# Revit family: Bath&ShowerMixer-(Built-in)-Vitra-JunoSeries-A40868
name_source: partatom
category: Plumbing Fixtures
revit_build: Autodesk Revit 2017 (Build: 20160225_1515(x64)
units: mm (PartAtom-declared; Revit-internal decimal feet)

## family parameters
Cut with Voids When Loaded = No
Host = Face
OmniClass Number = 23.45.00.00
OmniClass Title = Sanitary, Laundry, and Cleaning Equipment
Part Type = Normal
Room Calculation Point = No
Round Connector Dimension = Use Diameter
Shared = Yes

## types (3) — shared parameters
BIMobject category = Bath/Shower Mixer
Brand = VitrA
CW Connection = Yes
Connection Diameter (mm) = 15 mm
Default Elevation = 850 mm
Description = Juno Bath/Shower Mixer
Design country = Turkey
HW Connection = Yes
Hot Water Supply (max.) = 80 °C
Hot Water temperature, factory set to = 38 °C
IFC Classification = Sanitary Terminal
Main Material = Brass
Manufacturer = Vitra
Manufacturer name = Vitra
Masterformat 2014 Code = 22 40 00
Masterformat 2014 Description = Plumbing Fixtures
Min. flow pressure of = 0.5 bar
Mounting type = Built-In
NBS Referans Code = 45-35-70/315
NBS Referans Description = Water supply fittings for baths
Nominal Depth (mm) = 200 mm  [stored 0.656168 ft]
Nominal Height (mm) = 106 mm  [stored 0.347769 ft]
Nominal Width (mm) = 220 mm  [stored 0.721785 ft]
Number Of Connections = 2
OmniClass Code = 23.45.55.17
OmniClass Description = Mixing Faucets
Primary Material = <By Category>
Product Properties = Energy Saving
Product Type = Bath&Shower Mixer
Product certification = https://www.vitraglobal.com
Product family = Juno
Product group = Juno Bath&Shower Mixer
Product url = https://www.vitra.com.tr
Range of Hot Water Supply = 5 - 65 °C
Range of flow pressure = 1 - 5 bar
Technical description = https://www.vitra.com.tr
Test Pressure = 16 bar
URL = https://vitraglobal.com
Uniclass 1.4 Code = L725111
Uniclass 1.4 Description = Mixer taps
Uniclass 2.0 Code = Pr_40_20_87_09
Uniclass 2.0 Description = Bath taps
Uniclass 2015 Code = Pr_40_20_87_09
Uniclass 2015 Name = Bath taps
Uniformat II Code = 22 40 00
Uniformat II Description = Plumbing Fixture
Vent Connection = No
Warranty Period (Year) = 10 Years
Waste Connection = No
Youtube = https://www.youtube.com

## per-type parameters (varying)
| type | Article No. (default) | Coating Material | Color | Model | Product SKU |
| Bath&ShowerMixer-Vitra-JunoSeries-A40868 | A40868 | Chrome | Chrome | A40868 | A40868 |
| Bath&ShowerMixer-Vitra-JunoSeries-A4086823 | A4086823 | Gold | Gold | A4086823 | A4086823 |
| Bath&ShowerMixer-Vitra-JunoSeries-A4086826 | A4086826 | BrightCopper | Copper | A4086826 | A4086826 |

note: [stored X ft] marks values corroborated as IEEE doubles in the binary element streams (Revit-internal decimal feet)

## geometry (parser evidence)
native form markers: Blend x2, Sweep x3
no freeform markers — native parametric forms only
